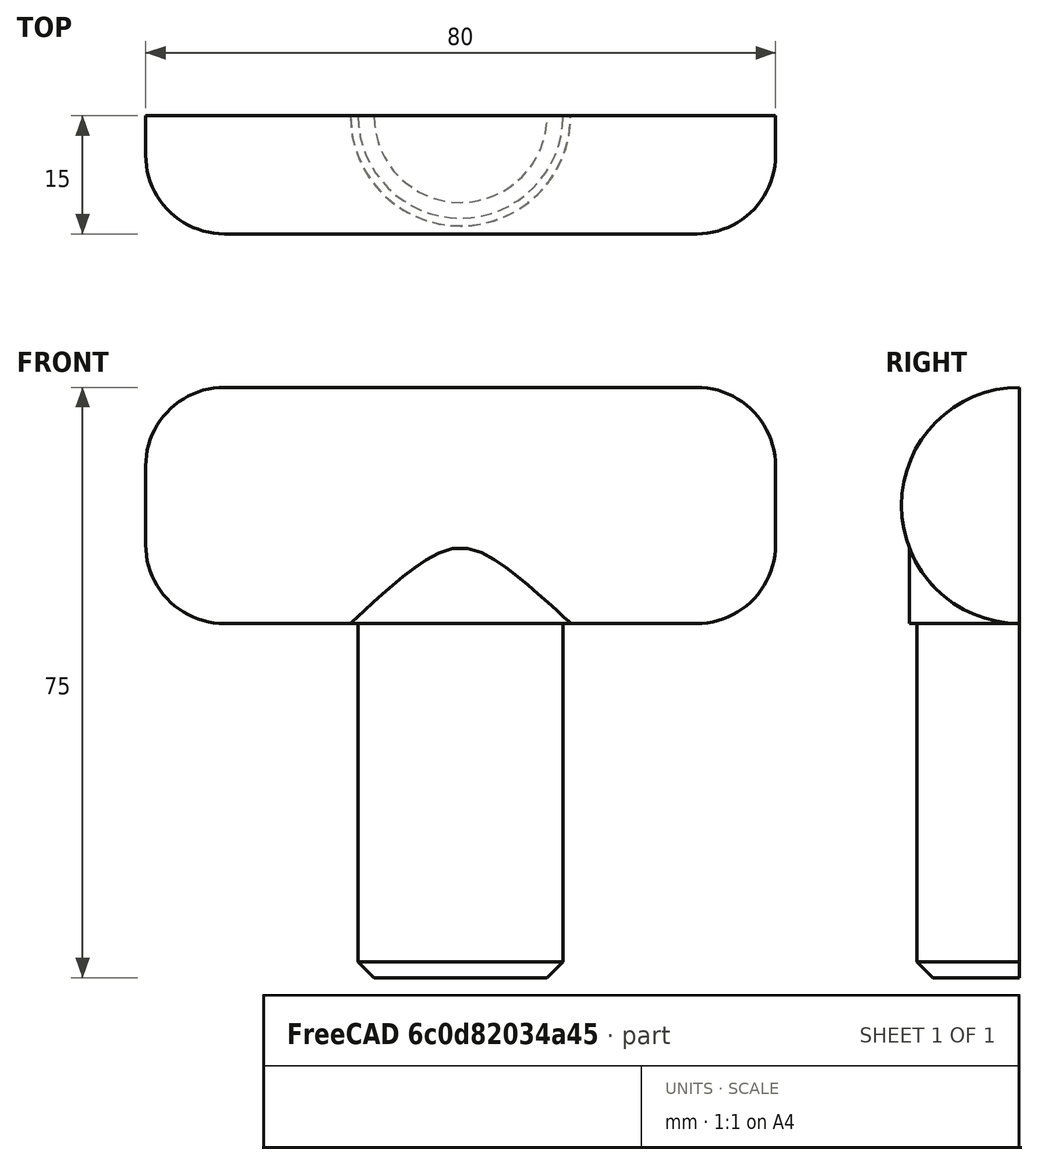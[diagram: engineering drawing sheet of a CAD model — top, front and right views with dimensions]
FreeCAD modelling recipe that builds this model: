
FCSTD DOCUMENT  (FreeCAD 0.20R29603 (Git))
Label: lapat_nyel
License: All rights reserved
LicenseURL: http://en.wikipedia.org/wiki/All_rights_reserved
objects: PartDesign::AdditiveCylinder×3, PartDesign::Chamfer×1, PartDesign::Fillet×1, PartDesign::SubtractiveBox×1, PartDesign::Body×1
note: 13 computed .brp shape members not serialized (recipe doc carries the construction recipe); baked Part::Feature solids carry a one-line shape summary decoded from their .brp

FEATURE [PartDesign::AdditiveCylinder] Cylinder
  Angle = 360
  AttacherType = Attacher::AttachEngine3D
  FirstAngle = 0
  Height = 45
  Radius = 13
  SecondAngle = 0
FEATURE [PartDesign::AdditiveCylinder] Cylinder001
  Angle = 360
  AttacherType = Attacher::AttachEngine3D
  BaseFeature = -> Cylinder
  FirstAngle = 0
  Height = 10
  MapMode = 5
  Placement = pos=(0,0,45) rot=(0,0,1;0rad)
  Radius = 14
  SecondAngle = 0
  Support = -> [Cylinder]
FEATURE [PartDesign::AdditiveCylinder] Cylinder002
  Angle = 360
  AttacherType = Attacher::AttachEngine3D
  AttachmentOffset = pos=(0,60,-40) rot=(0,0,1;0rad)
  BaseFeature = -> Cylinder001
  FirstAngle = 0
  Height = 80
  MapMode = 5
  Placement = pos=(-40,2.22e-14,60) rot=(0.57735,0.57735,0.57735;2.0944rad)
  Radius = 15
  SecondAngle = 0
  Support = -> [YZ_Plane]
FEATURE [PartDesign::Chamfer] Chamfer
  Angle = 45
  Base = -> Cylinder002 [Edge12]
  BaseFeature = -> Cylinder002
  ChamferType = 0
  FlipDirection = false
  Placement = pos=(-40,2.22e-14,60) rot=(0.57735,0.57735,0.57735;2.0944rad)
  Size = 2
  Size2 = 1
  SupportTransform = false
  UseAllEdges = false
FEATURE [PartDesign::Fillet] Fillet
  Base = -> Chamfer [Edge15,Edge13]
  BaseFeature = -> Chamfer
  Placement = pos=(-40,2.22e-14,60) rot=(0.57735,0.57735,0.57735;2.0944rad)
  Radius = 10
  SupportTransform = false
  UseAllEdges = false
FEATURE [PartDesign::SubtractiveBox] Box
  AttacherType = Attacher::AttachEngine3D
  AttachmentOffset = pos=(-40,0,-15) rot=(0,0,1;0rad)
  BaseFeature = -> Fillet
  Height = 15
  Length = 80
  MapMode = 5
  Placement = pos=(-40,15,3.3e-15) rot=(1,0,0;1.5708rad)
  Support = -> [XZ_Plane]
  Width = 80
FEATURE [PartDesign::Body] Body
  Group = -> [Cylinder,Cylinder001,Cylinder002,Chamfer,Fillet,Box]
  Origin = -> Origin
  Tip = -> Box
